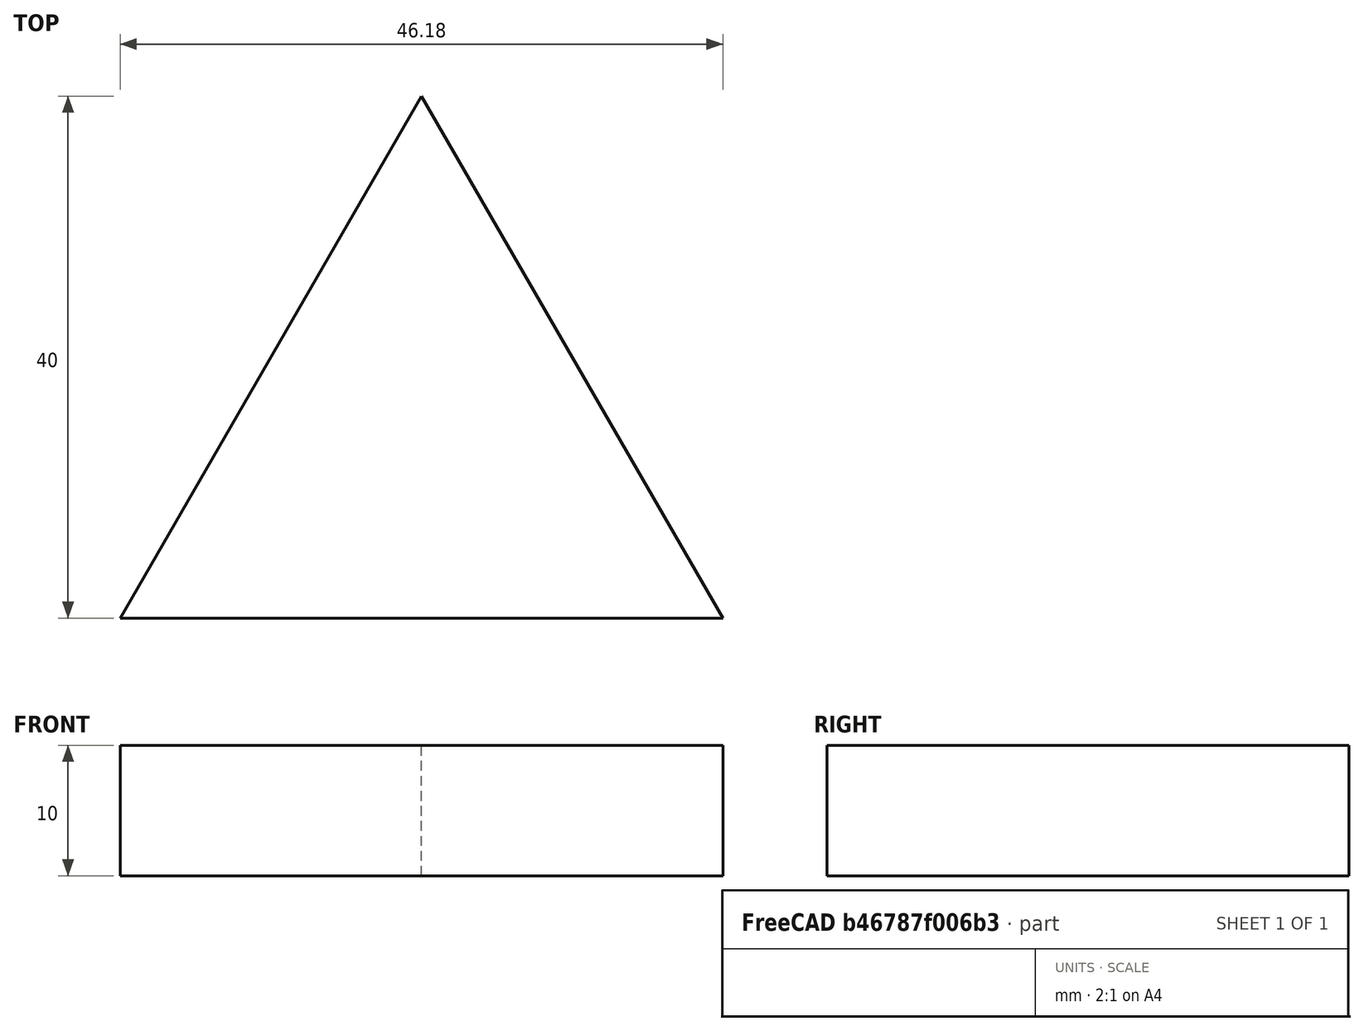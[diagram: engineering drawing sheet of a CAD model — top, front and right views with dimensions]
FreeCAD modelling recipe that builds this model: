
FCSTD DOCUMENT  (FreeCAD 0.21R33694 (Git))
Label: OJT1_T20P01.tri
License: All rights reserved
LicenseURL: http://en.wikipedia.org/wiki/All_rights_reserved
objects: Sketcher::SketchObject×1, PartDesign::Pad×1, PartDesign::Body×1, App::Part×1
note: 4 computed .brp shape members not serialized (recipe doc carries the construction recipe); baked Part::Feature solids carry a one-line shape summary decoded from their .brp

FEATURE [Sketcher::SketchObject] Sketch
  FullyConstrained = true
  MapMode = 5
  Support = -> [XY_Plane001]
  sketch-geometry (4):
    g0: LineSegment StartX=-23.094 StartY=-20 StartZ=0 EndX=0 EndY=20 EndZ=0
    g1: LineSegment StartX=0 StartY=20 StartZ=0 EndX=23.094 EndY=-20 EndZ=0
    g2: LineSegment StartX=23.094 StartY=-20 StartZ=0 EndX=-23.094 EndY=-20 EndZ=0
    g3: LineSegment StartX=0 StartY=20 StartZ=0 EndX=0 EndY=-20 EndZ=0
  constraints (10):
    c: Coincident(g0,g1)
    c: Coincident(g1,g2)
    c: Coincident(g2,g0)
    c: PointOnObject(g3,g2)
    c: Coincident(g0,g3)
    c: PointOnObject(g0,g-2)
    c: Symmetric(g3,g0,g-1)
    c: Symmetric(g1,g0,g-2)
    c: Angle(g2,g0) = 1.0472
    c: DistanceY(g3,g3) = 40
FEATURE [PartDesign::Pad] Pad
  Direction = (0,0,1)
  Length = 10
  Length2 = 10
  Profile = -> Sketch
  ReferenceAxis = -> Sketch [N_Axis]
  Refine = true
  Type = 0
FEATURE [PartDesign::Body] Body
  Group = -> [Sketch,Pad]
  Origin = -> Origin001
  Tip = -> Pad
FEATURE [App::Part] Part
  Group = -> [Body]
  Origin = -> Origin
